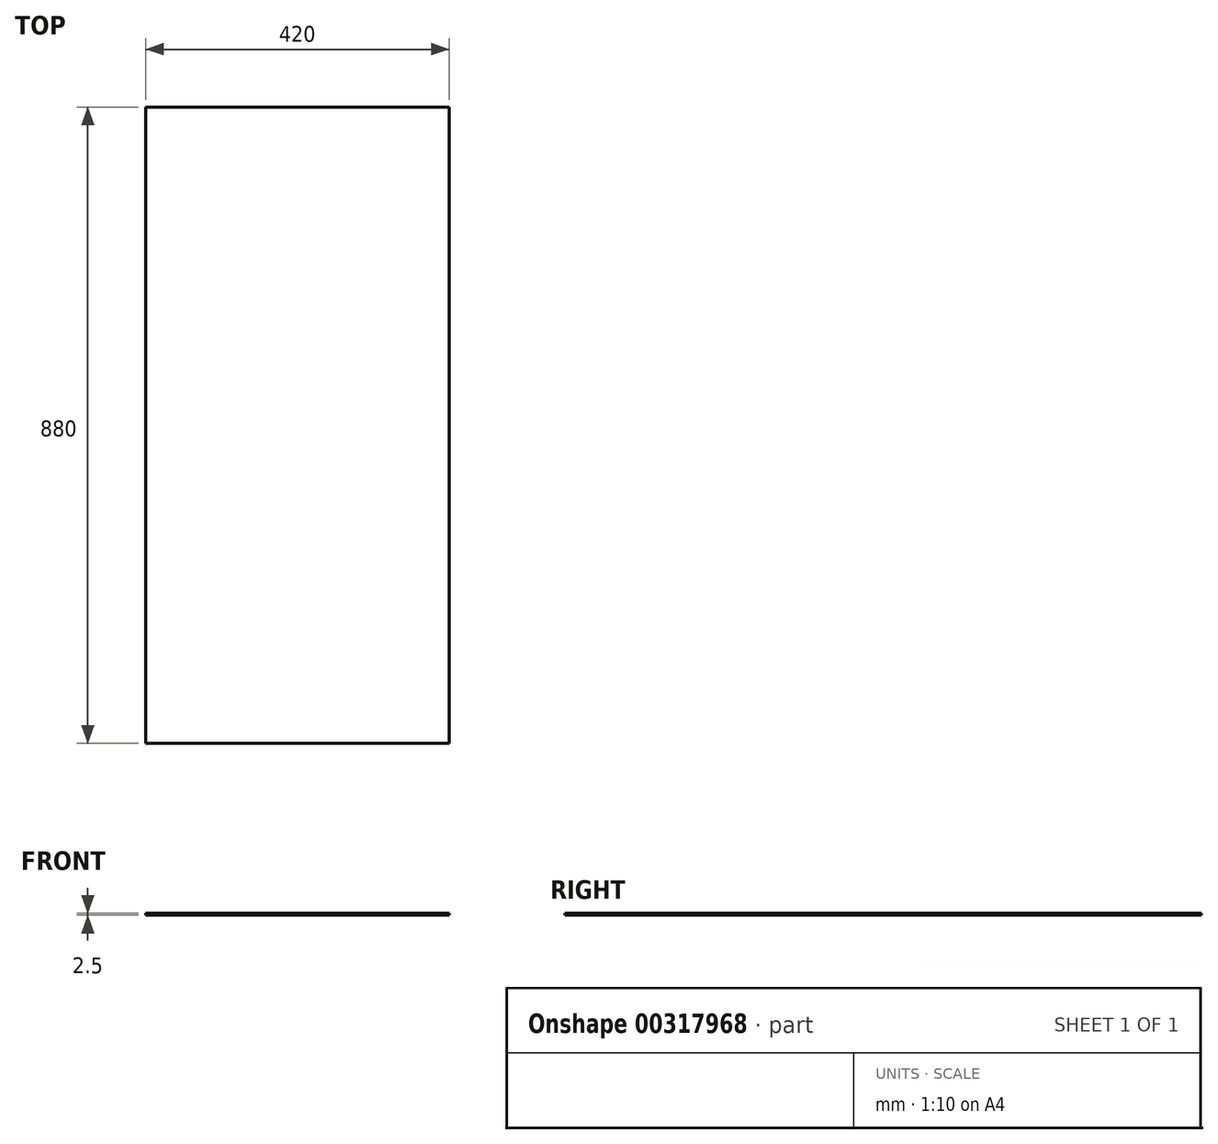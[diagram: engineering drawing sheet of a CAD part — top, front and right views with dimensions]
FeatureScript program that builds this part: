
annotation { "Feature Type Name" : "Feature", "Feature Type Description" : "" }
export const myFeature = defineFeature(function(context is Context, id is Id, definition is map)
    precondition{}
    {
        {
            var Q0;
            Q0=qCreatedBy(makeId("Top.planeOp"),FACE);
            var sketch = newSketch(context, id + "F0", { "sketchPlane" : qUnion([Q0])});
            skLineSegment(sketch, "E0.bottom", {"start": v(210, 440) * mm, "end": v(-210, 440) * mm});
            skLineSegment(sketch, "E0.top", {"start": v(210, -440) * mm, "end": v(-210, -440) * mm});
            skLineSegment(sketch, "E0.left", {"start": v(210, 440) * mm, "end": v(210, -440) * mm});
            skLineSegment(sketch, "E0.right", {"start": v(-210, 440) * mm, "end": v(-210, -440) * mm});
            skPoint(sketch, "E0.middle", {"position": v(0, 0) * mm});
            skSolve(sketch);
        }
        {
            var Q0;
            Q0 = qSketchRegion(id + "F0", true);
            extrude(context, id + "F1", {"entities" : qUnion([Q0]), "endBound" : BoundingType.SYMMETRIC, "depth" : 2.5 * mm});
        }
    });
